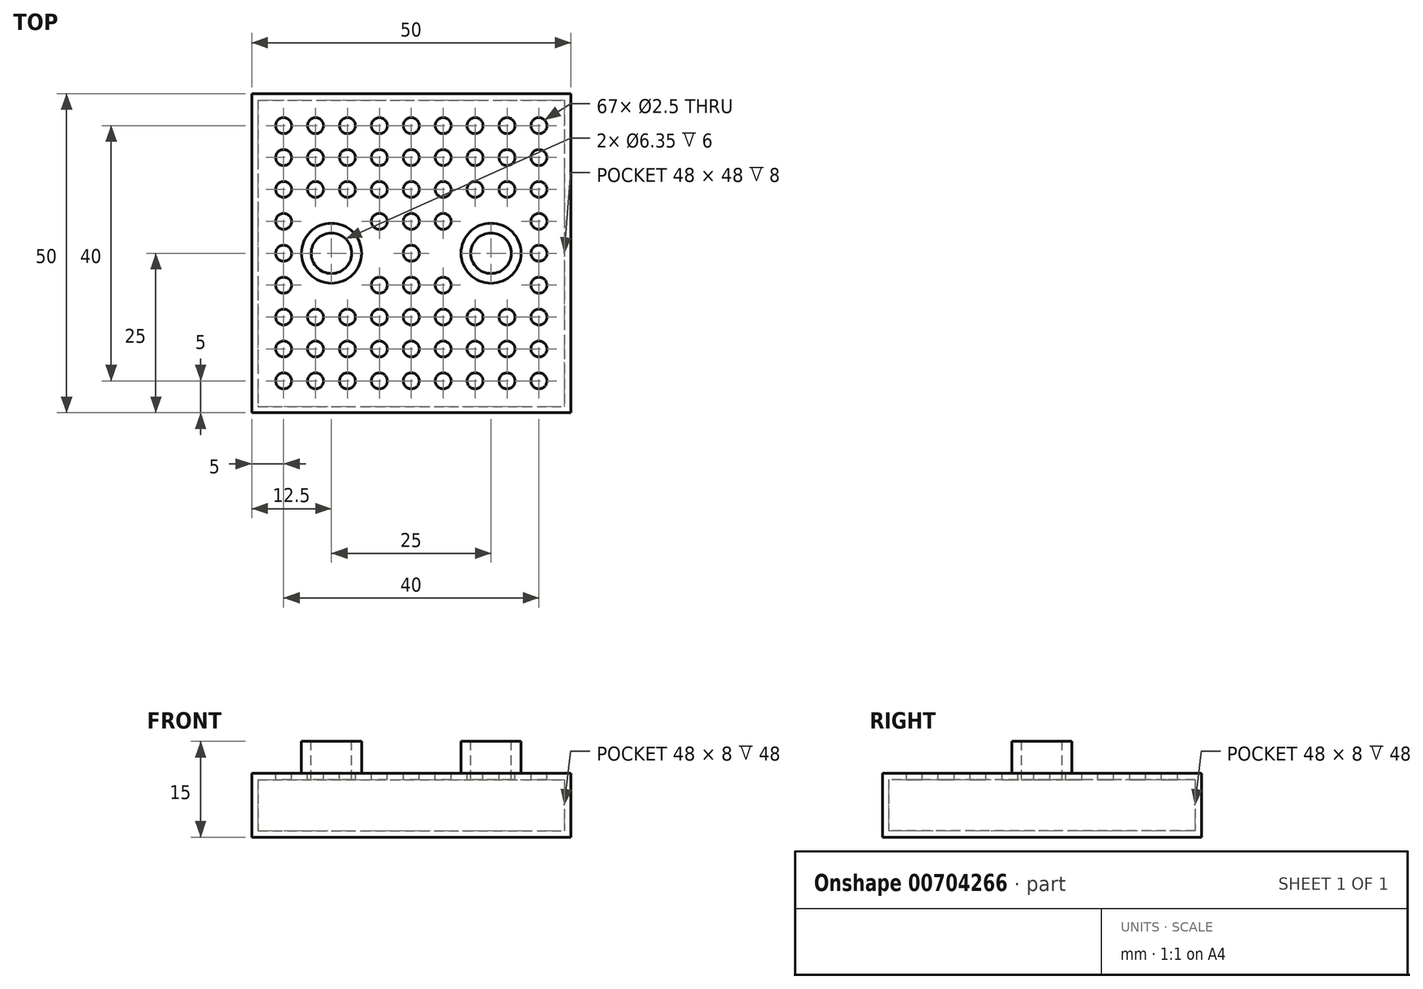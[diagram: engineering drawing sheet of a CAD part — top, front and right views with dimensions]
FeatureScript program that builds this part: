
annotation { "Feature Type Name" : "Feature", "Feature Type Description" : "" }
export const myFeature = defineFeature(function(context is Context, id is Id, definition is map)
    precondition{}
    {
        {
            var Q0;
            Q0=qCreatedBy(makeId("Top.planeOp"),FACE);
            var sketch = newSketch(context, id + "F0", { "sketchPlane" : qUnion([Q0])});
            skLineSegment(sketch, "E0.bottom", {"start": v(-25, 25) * mm, "end": v(25, 25) * mm});
            skLineSegment(sketch, "E0.top", {"start": v(-25, -25) * mm, "end": v(25, -25) * mm});
            skLineSegment(sketch, "E0.left", {"start": v(-25, 25) * mm, "end": v(-25, -25) * mm});
            skLineSegment(sketch, "E0.right", {"start": v(25, 25) * mm, "end": v(25, -25) * mm});
            skSolve(sketch);
        }
        {
            var Q0;
            Q0=makeQuery(id+"F0.imprint","IMPRINT",FACE,{"disambiguationData":[TD([[makeQuery(id+"F0.imprint","IMPRINT",EDGE,{"derivedFrom":sQuery(id+"F0.wireOp",EDGE,"E0.bottom")}),-1.0]])]});
            extrude(context, id + "F1", {"entities" : qUnion([Q0]), "depth" : 10 * mm, "offsetDistance" : 25 * mm});
        }
        {
            var Q0;
            Q0=makeQuery(id+"F1.opExtrude","CAP_FACE",FACE,{"disambiguationData":[OSD([sQuery(id+"F0.wireOp",EDGE,"E0.bottom"),sQuery(id+"F0.wireOp",EDGE,"E0.top"),sQuery(id+"F0.wireOp",EDGE,"E0.left"),sQuery(id+"F0.wireOp",EDGE,"E0.right")])],"isStart":false});
            var Q1;
            Q1=makeQuery(id+"F1.opExtrude","SWEPT_BODY",BODY,{"disambiguationData":[OSD([sQuery(id+"F0.wireOp",EDGE,"E0.bottom"),sQuery(id+"F0.wireOp",EDGE,"E0.top"),sQuery(id+"F0.wireOp",EDGE,"E0.left"),sQuery(id+"F0.wireOp",EDGE,"E0.right")])]});
            shell(context, id + "F2", {"isHollow" : true, "entities" : qUnion([Q0]), "parts" : qUnion([Q1]), "thickness" : 1 * mm});
        }
        {
            var Q0;
            Q0=makeQuery(id+"F1.opExtrude","CAP_FACE",FACE,{"disambiguationData":[OSD([sQuery(id+"F0.wireOp",EDGE,"E0.bottom"),sQuery(id+"F0.wireOp",EDGE,"E0.top"),sQuery(id+"F0.wireOp",EDGE,"E0.left"),sQuery(id+"F0.wireOp",EDGE,"E0.right")])],"isStart":false});
            var sketch = newSketch(context, id + "F3", { "sketchPlane" : qUnion([Q0])});
            skCircle(sketch, "E1", {"center": v(-12.5, 0) * mm, "radius": 3.17 * mm});
            skCircle(sketch, "E2", {"center": v(12.5, 0) * mm, "radius": 3.17 * mm});
            skSolve(sketch);
        }
        {
            var Q0;
            Q0=makeQuery(id+"F3.imprint","IMPRINT",FACE,{"disambiguationData":[TD([[makeQuery(id+"F3.imprint","IMPRINT",EDGE,{"derivedFrom":sQuery(id+"F3.wireOp",EDGE,"E2")}),1.0]])]});
            var Q1;
            Q1=makeQuery(id+"F3.imprint","IMPRINT",FACE,{"disambiguationData":[TD([[makeQuery(id+"F3.imprint","IMPRINT",EDGE,{"derivedFrom":sQuery(id+"F3.wireOp",EDGE,"E1")}),1.0]])]});
            extrude(context, id + "F4", {"entities" : qUnion([Q0, Q1]), "operationType" : NewBodyOperationType.REMOVE, "oppositeDirection" : true, "depth" : 2 * mm, "offsetDistance" : 25 * mm});
        }
        {
            var Q0;
            Q0=makeQuery(id+"F1.opExtrude","CAP_FACE",FACE,{"disambiguationData":[OSD([sQuery(id+"F0.wireOp",EDGE,"E0.bottom"),sQuery(id+"F0.wireOp",EDGE,"E0.top"),sQuery(id+"F0.wireOp",EDGE,"E0.left"),sQuery(id+"F0.wireOp",EDGE,"E0.right")])],"isStart":false});
            var sketch = newSketch(context, id + "F5", { "sketchPlane" : qUnion([Q0])});
            skCircle(sketch, "E3", {"center": v(-12.5, 0) * mm, "radius": 3.17 * mm});
            skCircle(sketch, "E4", {"center": v(-12.5, 0) * mm, "radius": 4.7 * mm});
            skCircle(sketch, "E5", {"center": v(12.5, 0) * mm, "radius": 3.17 * mm});
            skCircle(sketch, "E6", {"center": v(12.5, 0) * mm, "radius": 4.7 * mm});
            skSolve(sketch);
        }
        {
            var Q0;
            Q0=makeQuery(id+"F5.imprint","IMPRINT",FACE,{"disambiguationData":[TD([[makeQuery(id+"F5.imprint","IMPRINT",EDGE,{"derivedFrom":sQuery(id+"F5.wireOp",EDGE,"E3")}),-1.0]])]});
            var Q1;
            Q1=makeQuery(id+"F5.imprint","IMPRINT",FACE,{"disambiguationData":[TD([[makeQuery(id+"F5.imprint","IMPRINT",EDGE,{"derivedFrom":sQuery(id+"F5.wireOp",EDGE,"E5")}),-1.0]])]});
            extrude(context, id + "F6", {"entities" : qUnion([Q0, Q1]), "operationType" : NewBodyOperationType.ADD, "depth" : 5 * mm, "offsetDistance" : 25 * mm});
        }
        {
            var Q0;
            Q0=makeQuery(id+"F1.opExtrude","CAP_FACE",FACE,{"disambiguationData":[OSD([sQuery(id+"F0.wireOp",EDGE,"E0.bottom"),sQuery(id+"F0.wireOp",EDGE,"E0.top"),sQuery(id+"F0.wireOp",EDGE,"E0.left"),sQuery(id+"F0.wireOp",EDGE,"E0.right")])],"isStart":false});
            var sketch = newSketch(context, id + "F7", { "sketchPlane" : qUnion([Q0])});
            skCircle(sketch, "E7", {"center": v(-20, 20) * mm, "radius": 1.25 * mm});
            skCircle(sketch, "E8", {"center": v(-15, 20) * mm, "radius": 1.25 * mm});
            skCircle(sketch, "E9.2.0.0", {"center": v(-10, 20) * mm, "radius": 1.25 * mm});
            skCircle(sketch, "E9.3.0.0", {"center": v(-5, 20) * mm, "radius": 1.25 * mm});
            skCircle(sketch, "E9.4.0.0", {"center": v(0, 20) * mm, "radius": 1.25 * mm});
            skCircle(sketch, "E9.5.0.0", {"center": v(5, 20) * mm, "radius": 1.25 * mm});
            skCircle(sketch, "E9.6.0.0", {"center": v(10, 20) * mm, "radius": 1.25 * mm});
            skCircle(sketch, "E9.7.0.0", {"center": v(15, 20) * mm, "radius": 1.25 * mm});
            skCircle(sketch, "E9.8.0.0", {"center": v(20, 20) * mm, "radius": 1.25 * mm});
            skLineSegment(sketch, "E9.direction1", {"start": v(-20, 20) * mm, "end": v(-15, 20) * mm, "construction": true});
            skLineSegment(sketch, "E10", {"start": v(-20, 20) * mm, "end": v(-20, 17.5) * mm});
            skLineSegment(sketch, "E11", {"start": v(-20, 17.5) * mm, "end": v(20, 17.5) * mm});
            skCircle(sketch, "E12.MirrorC", {"center": v(-20, 15) * mm, "radius": 1.25 * mm});
            skCircle(sketch, "E13.MirrorC", {"center": v(-15, 15) * mm, "radius": 1.25 * mm});
            skCircle(sketch, "E14.MirrorC", {"center": v(-10, 15) * mm, "radius": 1.25 * mm});
            skCircle(sketch, "E15.MirrorC", {"center": v(-5, 15) * mm, "radius": 1.25 * mm});
            skCircle(sketch, "E16.MirrorC", {"center": v(5, 15) * mm, "radius": 1.25 * mm});
            skCircle(sketch, "E17.MirrorC", {"center": v(10, 15) * mm, "radius": 1.25 * mm});
            skCircle(sketch, "E18.MirrorC", {"center": v(0, 15) * mm, "radius": 1.25 * mm});
            skCircle(sketch, "E19.MirrorC", {"center": v(15, 15) * mm, "radius": 1.25 * mm});
            skCircle(sketch, "E20.MirrorC", {"center": v(20, 15) * mm, "radius": 1.25 * mm});
            skLineSegment(sketch, "E21", {"start": v(-20, 17.5) * mm, "end": v(-20, 12.5) * mm});
            skLineSegment(sketch, "E22", {"start": v(-20, 12.5) * mm, "end": v(20, 12.5) * mm});
            skCircle(sketch, "E23.MirrorC", {"center": v(-20, 10) * mm, "radius": 1.25 * mm});
            skCircle(sketch, "E24.MirrorC", {"center": v(-15, 10) * mm, "radius": 1.25 * mm});
            skCircle(sketch, "E25.MirrorC", {"center": v(-10, 10) * mm, "radius": 1.25 * mm});
            skCircle(sketch, "E26.MirrorC", {"center": v(-5, 10) * mm, "radius": 1.25 * mm});
            skCircle(sketch, "E27.MirrorC", {"center": v(0, 10) * mm, "radius": 1.25 * mm});
            skCircle(sketch, "E28.MirrorC", {"center": v(10, 10) * mm, "radius": 1.25 * mm});
            skCircle(sketch, "E29.MirrorC", {"center": v(15, 10) * mm, "radius": 1.25 * mm});
            skCircle(sketch, "E30.MirrorC", {"center": v(5, 10) * mm, "radius": 1.25 * mm});
            skCircle(sketch, "E31.MirrorC", {"center": v(20, 10) * mm, "radius": 1.25 * mm});
            skLineSegment(sketch, "E32", {"start": v(-20, 12.5) * mm, "end": v(-20, 7.5) * mm});
            skLineSegment(sketch, "E33", {"start": v(-20, 7.5) * mm, "end": v(20, 7.5) * mm});
            skCircle(sketch, "E34.MirrorC", {"center": v(-20, 5) * mm, "radius": 1.25 * mm});
            skCircle(sketch, "E35.MirrorC", {"center": v(-5, 5) * mm, "radius": 1.25 * mm});
            skCircle(sketch, "E36.MirrorC", {"center": v(0, 5) * mm, "radius": 1.25 * mm});
            skCircle(sketch, "E37.MirrorC", {"center": v(5, 5) * mm, "radius": 1.25 * mm});
            skCircle(sketch, "E38.MirrorC", {"center": v(20, 5) * mm, "radius": 1.25 * mm});
            skLineSegment(sketch, "E39", {"start": v(-20, 7.5) * mm, "end": v(-20, 2.5) * mm});
            skLineSegment(sketch, "E40", {"start": v(-20, 2.5) * mm, "end": v(-20, -2.5) * mm});
            skLineSegment(sketch, "E41", {"start": v(-20, -2.5) * mm, "end": v(-20, -7.5) * mm});
            skLineSegment(sketch, "E42", {"start": v(-20, -7.5) * mm, "end": v(-20, -12.5) * mm});
            skPoint(sketch, "E42.endSnap0", {"position": v(-20, -5) * mm});
            skLineSegment(sketch, "E43", {"start": v(-20, -12.5) * mm, "end": v(-20, -17.5) * mm});
            skLineSegment(sketch, "E44", {"start": v(-20, 2.5) * mm, "end": v(20, 2.5) * mm});
            skLineSegment(sketch, "E45", {"start": v(-20, -2.5) * mm, "end": v(20, -2.5) * mm});
            skLineSegment(sketch, "E46", {"start": v(-20, -7.5) * mm, "end": v(20, -7.5) * mm});
            skLineSegment(sketch, "E47", {"start": v(-20, -12.5) * mm, "end": v(20, -12.5) * mm});
            skLineSegment(sketch, "E48", {"start": v(-20, -17.5) * mm, "end": v(20, -17.5) * mm});
            skCircle(sketch, "E49.MirrorC", {"center": v(-20, 0) * mm, "radius": 1.25 * mm});
            skCircle(sketch, "E50.MirrorC", {"center": v(0, 0) * mm, "radius": 1.25 * mm});
            skCircle(sketch, "E51.MirrorC", {"center": v(20, 0) * mm, "radius": 1.25 * mm});
            skCircle(sketch, "E52.MirrorC", {"center": v(-20, -15) * mm, "radius": 1.25 * mm});
            skCircle(sketch, "E53.MirrorC", {"center": v(-15, -15) * mm, "radius": 1.25 * mm});
            skCircle(sketch, "E54.MirrorC", {"center": v(-10, -15) * mm, "radius": 1.25 * mm});
            skCircle(sketch, "E55.MirrorC", {"center": v(-5, -15) * mm, "radius": 1.25 * mm});
            skCircle(sketch, "E56.MirrorC", {"center": v(0, -15) * mm, "radius": 1.25 * mm});
            skCircle(sketch, "E57.MirrorC", {"center": v(5, -15) * mm, "radius": 1.25 * mm});
            skCircle(sketch, "E58.MirrorC", {"center": v(10, -15) * mm, "radius": 1.25 * mm});
            skCircle(sketch, "E59.MirrorC", {"center": v(15, -15) * mm, "radius": 1.25 * mm});
            skCircle(sketch, "E60.MirrorC", {"center": v(20, -15) * mm, "radius": 1.25 * mm});
            skCircle(sketch, "E61.MirrorC", {"center": v(-20, -20) * mm, "radius": 1.25 * mm});
            skCircle(sketch, "E62.MirrorC", {"center": v(-15, -20) * mm, "radius": 1.25 * mm});
            skCircle(sketch, "E63.MirrorC", {"center": v(-10, -20) * mm, "radius": 1.25 * mm});
            skCircle(sketch, "E64.MirrorC", {"center": v(-5, -20) * mm, "radius": 1.25 * mm});
            skCircle(sketch, "E65.MirrorC", {"center": v(0, -20) * mm, "radius": 1.25 * mm});
            skCircle(sketch, "E66.MirrorC", {"center": v(5, -20) * mm, "radius": 1.25 * mm});
            skCircle(sketch, "E67.MirrorC", {"center": v(10, -20) * mm, "radius": 1.25 * mm});
            skCircle(sketch, "E68.MirrorC", {"center": v(15, -20) * mm, "radius": 1.25 * mm});
            skCircle(sketch, "E69.MirrorC", {"center": v(20, -20) * mm, "radius": 1.25 * mm});
            skCircle(sketch, "E70.MirrorC", {"center": v(-20, -10) * mm, "radius": 1.25 * mm});
            skCircle(sketch, "E71.MirrorC", {"center": v(-15, -10) * mm, "radius": 1.25 * mm});
            skCircle(sketch, "E72.MirrorC", {"center": v(-10, -10) * mm, "radius": 1.25 * mm});
            skCircle(sketch, "E73.MirrorC", {"center": v(-5, -10) * mm, "radius": 1.25 * mm});
            skCircle(sketch, "E74.MirrorC", {"center": v(0, -10) * mm, "radius": 1.25 * mm});
            skCircle(sketch, "E75.MirrorC", {"center": v(5, -10) * mm, "radius": 1.25 * mm});
            skCircle(sketch, "E76.MirrorC", {"center": v(10, -10) * mm, "radius": 1.25 * mm});
            skCircle(sketch, "E77.MirrorC", {"center": v(15, -10) * mm, "radius": 1.25 * mm});
            skCircle(sketch, "E78.MirrorC", {"center": v(20, -10) * mm, "radius": 1.25 * mm});
            skCircle(sketch, "E79.MirrorC", {"center": v(-20, -5) * mm, "radius": 1.25 * mm});
            skCircle(sketch, "E80.MirrorC", {"center": v(-5, -5) * mm, "radius": 1.25 * mm});
            skCircle(sketch, "E81.MirrorC", {"center": v(0, -5) * mm, "radius": 1.25 * mm});
            skCircle(sketch, "E82.MirrorC", {"center": v(5, -5) * mm, "radius": 1.25 * mm});
            skCircle(sketch, "E83.MirrorC", {"center": v(20, -5) * mm, "radius": 1.25 * mm});
            skSolve(sketch);
        }
        {
            var Q0;
            Q0 = qSketchRegion(id + "F7", true);
            extrude(context, id + "F8", {"entities" : qUnion([Q0]), "operationType" : NewBodyOperationType.REMOVE, "oppositeDirection" : true, "depth" : 1.5 * mm, "offsetDistance" : 25 * mm});
        }
    });
